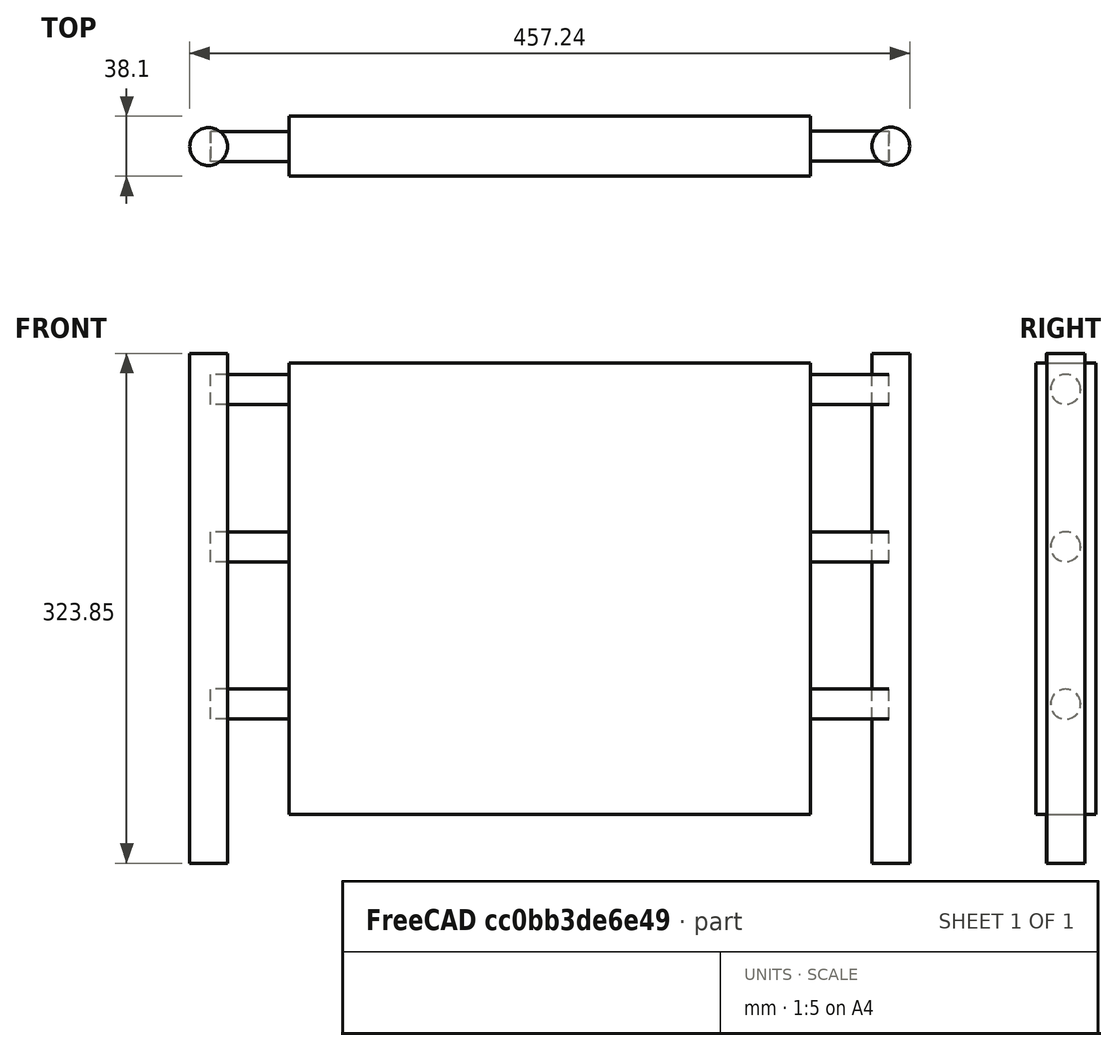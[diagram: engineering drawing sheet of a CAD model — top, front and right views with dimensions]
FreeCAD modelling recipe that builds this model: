
FCSTD DOCUMENT  (FreeCAD 0.16R6710 (Git))
Label: Task 1
License: All rights reserved
LicenseURL: http://en.wikipedia.org/wiki/All_rights_reserved
objects: Part::Cylinder×8, Part::Box×1
note: 9 computed .brp shape members not serialized (recipe doc carries the construction recipe); baked Part::Feature solids carry a one-line shape summary decoded from their .brp

FEATURE [Part::Box] Box  label="Cube"
  Height = 286.84
  Length = 331.14
  Width = 38.1
FEATURE [Part::Cylinder] Cylinder
  Angle = 360
  Height = 323.85
  Placement = pos=(382.222,19.1367,-31.0403) rot=(0,0,1;0rad)
  Radius = 12
FEATURE [Part::Cylinder] Cylinder001
  Angle = 360
  Height = 50
  Placement = pos=(331.14,19.05,70) rot=(0,1,0;1.5708rad)
  Radius = 9.525
FEATURE [Part::Cylinder] Cylinder002
  Angle = 360
  Height = 50
  Placement = pos=(331.14,19.05,170) rot=(0,1,0;1.5708rad)
  Radius = 9.525
FEATURE [Part::Cylinder] Cylinder003
  Angle = 360
  Height = 50
  Placement = pos=(331.14,19.05,270) rot=(0,1,0;1.5708rad)
  Radius = 9.525
FEATURE [Part::Cylinder] Cylinder004
  Angle = 360
  Height = 323.85
  Placement = pos=(-51.0218,18.8633,-31.0403) rot=(0,0,1;3.14159rad)
  Radius = 12
FEATURE [Part::Cylinder] Cylinder005
  Angle = 360
  Height = 50
  Placement = pos=(0.06,18.95,170) rot=(-0.707107,0,0.707107;3.14159rad)
  Radius = 9.525
FEATURE [Part::Cylinder] Cylinder006
  Angle = 360
  Height = 50
  Placement = pos=(0.06,18.95,270) rot=(-0.707107,0,0.707107;3.14159rad)
  Radius = 9.525
FEATURE [Part::Cylinder] Cylinder007
  Angle = 360
  Height = 50
  Placement = pos=(0.06,18.95,70) rot=(-0.707107,0,0.707107;3.14159rad)
  Radius = 9.525
